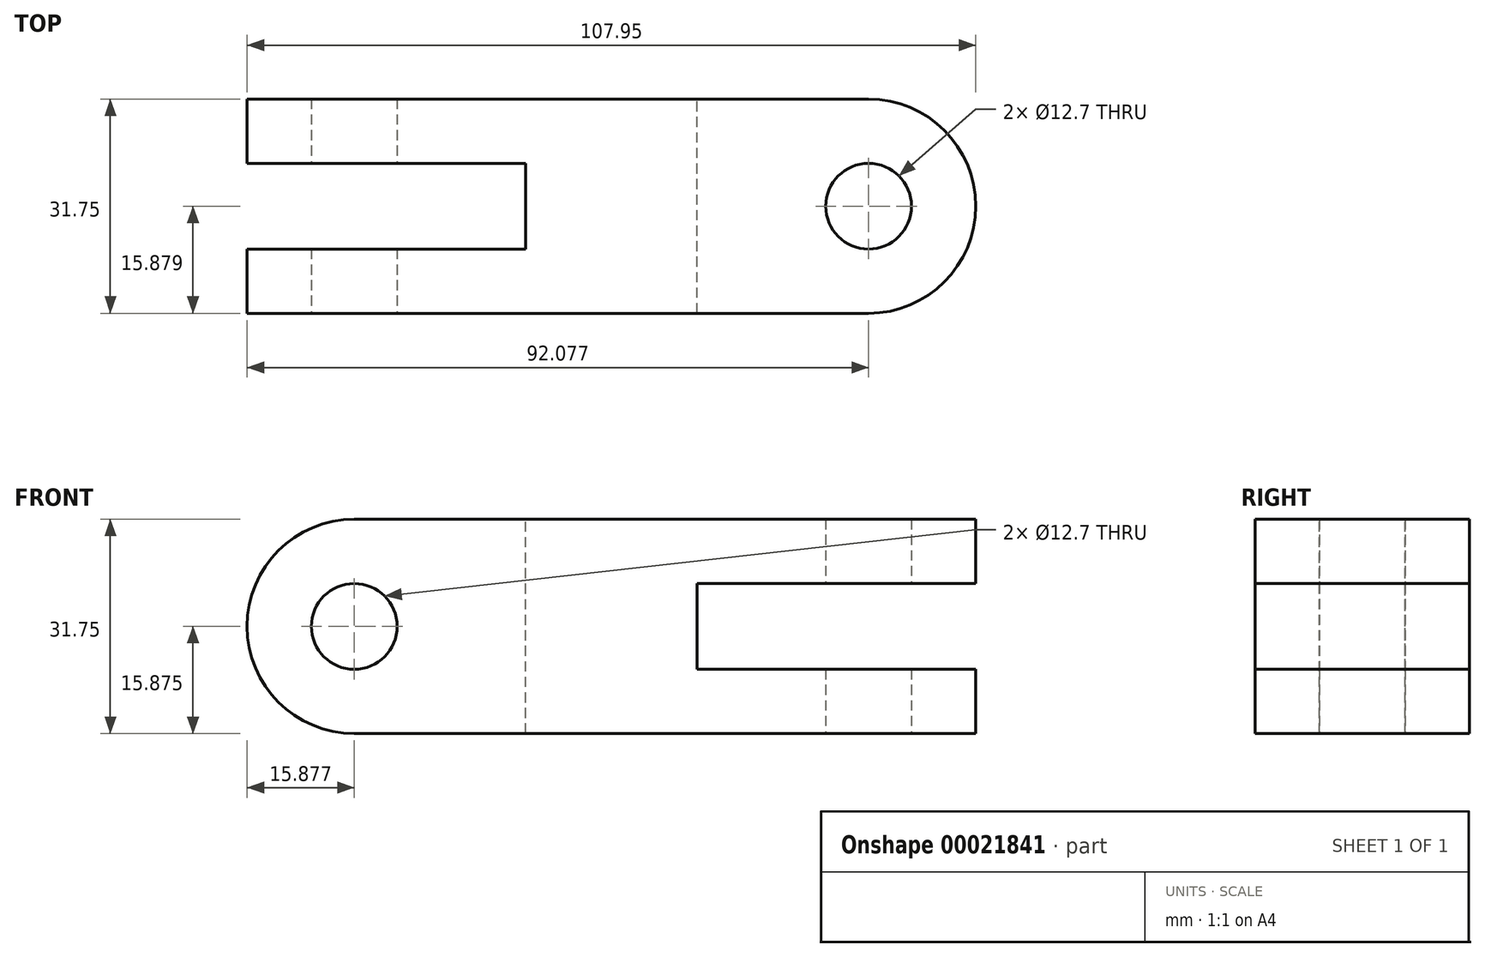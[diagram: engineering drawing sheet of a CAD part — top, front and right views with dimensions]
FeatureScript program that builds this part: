
annotation { "Feature Type Name" : "Feature", "Feature Type Description" : "" }
export const myFeature = defineFeature(function(context is Context, id is Id, definition is map)
    precondition{}
    {
        {
            var Q0;
            Q0=qCreatedBy(makeId("Top.planeOp"),FACE);
            var sketch = newSketch(context, id + "F0", { "sketchPlane" : qUnion([Q0])});
            skLineSegment(sketch, "E0.bottom", {"start": v(-41.05, 14.2) * mm, "end": v(35.15, 14.2) * mm});
            skLineSegment(sketch, "E0.top", {"start": v(-41.05, -17.55) * mm, "end": v(35.15, -17.55) * mm});
            skLineSegment(sketch, "E0.left", {"start": v(-41.05, 14.2) * mm, "end": v(-41.05, -17.55) * mm});
            skArc(sketch, "E1", {"start": v(35.15, -17.55) * mm, "mid": v(51.02, -1.67) * mm, "end": v(35.15, 14.2) * mm});
            skCircle(sketch, "E2", {"center": v(35.15, -1.67) * mm, "radius": 6.35 * mm});
            skSolve(sketch);
        }
        {
            var Q0;
            Q0 = qSketchRegion(id + "F0", true);
            extrude(context, id + "F1", {"entities" : qUnion([Q0]), "depth" : 31.75 * mm});
        }
        {
            var Q0;
            Q0=makeQuery(id+"F1.opExtrude","SWEPT_FACE",FACE,{"disambiguationData":[OSD([sQuery(id+"F0.wireOp",EDGE,"E0.top")])]});
            var sketch = newSketch(context, id + "F2", { "sketchPlane" : qUnion([Q0])});
            skArc(sketch, "E3", {"start": v(-41.05, 31.75) * mm, "mid": v(-56.93, 15.88) * mm, "end": v(-41.05, 0) * mm});
            skSolve(sketch);
        }
        {
            var Q0;
            Q0 = qSketchRegion(id + "F2", true);
            var Q1;
            {var subQ4=sQuery(id+"F2.wireOp",EDGE,"E3");Q1=makeQuery(id+"F2.imprint","IMPRINT",FACE,{"disambiguationData":[TD([[makeQuery(id+"F2.imprint","IMPRINT",EDGE,{"derivedFrom":subQ4}),1.0]])]});}
            extrude(context, id + "F3", {"entities" : qUnion([Q0, Q1]), "operationType" : NewBodyOperationType.ADD, "oppositeDirection" : true, "depth" : 31.75 * mm});
        }
        {
            var Q0;
            {var subQ0=sQuery(id+"F0.wireOp",EDGE,"E0.top");Q0=makeQuery(id+"F3.boolean.opBoolean","MERGE",FACE,{"derivedFrom":[makeQuery(id+"F1.opExtrude","SWEPT_FACE",FACE,{"disambiguationData":[OSD([subQ0])]}),makeQuery(id+"F3.opExtrude","CAP_FACE",FACE,{"disambiguationData":[OSD([subQ0,sQuery(id+"F0.wireOp",EDGE,"E0.left"),sQuery(id+"F2.wireOp",EDGE,"E3")])],"isStart":true})]});}
            var sketch = newSketch(context, id + "F4", { "sketchPlane" : qUnion([Q0])});
            skCircle(sketch, "E4", {"center": v(-41.05, 15.88) * mm, "radius": 6.35 * mm});
            skSolve(sketch);
        }
        {
            var Q0;
            Q0 = qSketchRegion(id + "F4", true);
            extrude(context, id + "F5", {"entities" : qUnion([Q0]), "operationType" : NewBodyOperationType.REMOVE, "oppositeDirection" : true, "depth" : 31.75 * mm});
        }
        {
            var Q0;
            Q0=makeQuery(id+"F1.opExtrude","CAP_FACE",FACE,{"disambiguationData":[OSD([sQuery(id+"F0.wireOp",EDGE,"E0.bottom"),sQuery(id+"F0.wireOp",EDGE,"E0.top"),sQuery(id+"F0.wireOp",EDGE,"E0.left"),sQuery(id+"F0.wireOp",EDGE,"E1"),sQuery(id+"F0.wireOp",EDGE,"E2")])],"isStart":false});
            var sketch = newSketch(context, id + "F6", { "sketchPlane" : qUnion([Q0])});
            skLineSegment(sketch, "E5", {"start": v(-41.05, -1.67) * mm, "end": v(-15.65, -1.67) * mm, "construction": true});
            skLineSegment(sketch, "E6", {"start": v(-15.65, -17.55) * mm, "end": v(-15.65, -8.02) * mm, "construction": true});
            skLineSegment(sketch, "E7.bottom", {"start": v(-15.65, -8.02) * mm, "end": v(-66.34, -8.02) * mm});
            skLineSegment(sketch, "E7.top", {"start": v(-15.65, 4.68) * mm, "end": v(-66.34, 4.68) * mm});
            skLineSegment(sketch, "E7.left", {"start": v(-15.65, -8.02) * mm, "end": v(-15.65, 4.68) * mm});
            skLineSegment(sketch, "E7.right", {"start": v(-66.34, -8.02) * mm, "end": v(-66.34, 4.68) * mm});
            skSolve(sketch);
        }
        {
            var Q0;
            Q0 = qSketchRegion(id + "F6", true);
            extrude(context, id + "F7", {"entities" : qUnion([Q0]), "operationType" : NewBodyOperationType.REMOVE, "oppositeDirection" : true, "depth" : 31.75 * mm});
        }
        {
            var Q0;
            Q0=makeQuery(id+"F3.boolean.opBoolean","MERGE",FACE,{"derivedFrom":[makeQuery(id+"F1.opExtrude","SWEPT_FACE",FACE,{"disambiguationData":[OSD([sQuery(id+"F0.wireOp",EDGE,"E0.bottom")])]}),makeQuery(id+"F3.opExtrude","CAP_FACE",FACE,{"disambiguationData":[OSD([sQuery(id+"F0.wireOp",EDGE,"E0.top"),sQuery(id+"F0.wireOp",EDGE,"E0.left"),sQuery(id+"F2.wireOp",EDGE,"E3")])],"isStart":false})]});
            var sketch = newSketch(context, id + "F8", { "sketchPlane" : qUnion([Q0])});
            skLineSegment(sketch, "E8", {"start": v(-35.15, 15.88) * mm, "end": v(-9.75, 15.88) * mm, "construction": true});
            skLineSegment(sketch, "E9", {"start": v(-9.75, 31.75) * mm, "end": v(-9.75, 22.23) * mm, "construction": true});
            skLineSegment(sketch, "E10.bottom", {"start": v(-9.75, 22.23) * mm, "end": v(-57.46, 22.23) * mm});
            skLineSegment(sketch, "E10.top", {"start": v(-9.75, 9.52) * mm, "end": v(-57.46, 9.52) * mm});
            skLineSegment(sketch, "E10.left", {"start": v(-9.75, 22.23) * mm, "end": v(-9.75, 9.52) * mm});
            skLineSegment(sketch, "E10.right", {"start": v(-57.46, 22.23) * mm, "end": v(-57.46, 9.52) * mm});
            skSolve(sketch);
        }
        {
            var Q0;
            Q0 = qSketchRegion(id + "F8", true);
            extrude(context, id + "F9", {"entities" : qUnion([Q0]), "operationType" : NewBodyOperationType.REMOVE, "endBound" : BoundingType.THROUGH_ALL, "oppositeDirection" : true, "depth" : 25.4 * mm});
        }
    });
